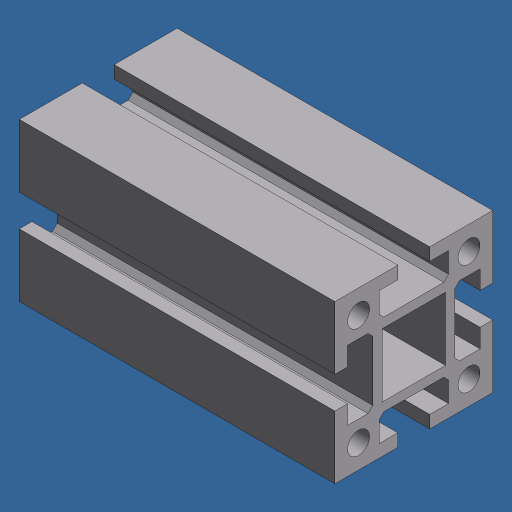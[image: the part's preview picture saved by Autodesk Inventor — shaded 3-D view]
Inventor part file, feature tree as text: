
AUTODESK INVENTOR PART (.ipt)
format: ipt  version: 2024.3 (Build 283343000, 343)  size: 158,208 bytes
history: native  units: mm (DEFAULTED — no unit token found)
features: other x5, extrude x1, sketch x1
ambient origin geometry x8: Origin, YZ Plane, XZ Plane, XY Plane, X Axis, Y Axis, Z Axis, Center Point
bodies: Body1 (feature_tree)
feature tree (7):
  other  "Finish - None"
  other  "Work Point1"
  other  "Work Point2"
  other  "Work Point3"
  other  "Work Axis1"
  extrude  "MK, 50MM"  [1 undecoded]
  sketch  "Skizze_1"  dims[d0=100.0mm d1=0.0mm]
note: 1 required parameter value undecoded (feature->parameter linkage not recoverable at this tier; creation-order binding heuristic only, values carry confidence <= 0.55)
